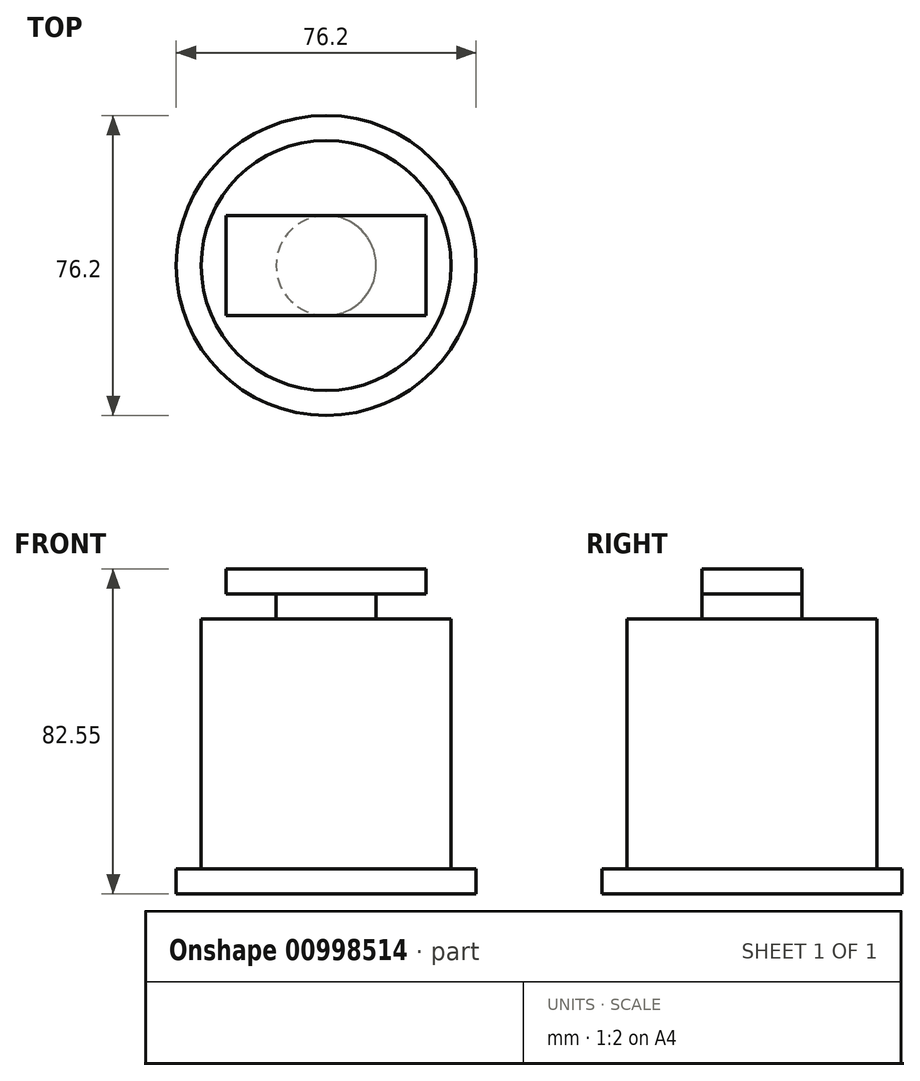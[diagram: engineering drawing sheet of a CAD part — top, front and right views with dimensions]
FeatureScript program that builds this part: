
annotation { "Feature Type Name" : "Feature", "Feature Type Description" : "" }
export const myFeature = defineFeature(function(context is Context, id is Id, definition is map)
    precondition{}
    {
        {
            var Q0;
            Q0=qCreatedBy(makeId("Top.planeOp"),FACE);
            var sketch = newSketch(context, id + "F0", { "sketchPlane" : qUnion([Q0])});
            skCircle(sketch, "E0", {"center": v(0, 0) * mm, "radius": 38.1 * mm});
            skSolve(sketch);
        }
        {
            var Q0;
            Q0=makeQuery(id+"F0.imprint","IMPRINT",FACE,{"disambiguationData":[TD([[makeQuery(id+"F0.imprint","IMPRINT",EDGE,{"derivedFrom":sQuery(id+"F0.wireOp",EDGE,"E0")}),1.0]])]});
            extrude(context, id + "F1", {"entities" : qUnion([Q0]), "depth" : 6.35 * mm, "offsetDistance" : 25.4 * mm});
        }
        {
            var Q0;
            Q0=makeQuery(id+"F1.opExtrude","CAP_FACE",FACE,{"disambiguationData":[OSD([sQuery(id+"F0.wireOp",EDGE,"E0")])],"isStart":false});
            var sketch = newSketch(context, id + "F2", { "sketchPlane" : qUnion([Q0])});
            skCircle(sketch, "E1", {"center": v(0, 0) * mm, "radius": 31.75 * mm});
            skSolve(sketch);
        }
        {
            var Q0;
            Q0=makeQuery(id+"F2.imprint","IMPRINT",FACE,{"disambiguationData":[TD([[makeQuery(id+"F2.imprint","IMPRINT",EDGE,{"derivedFrom":sQuery(id+"F2.wireOp",EDGE,"E1")}),1.0]])]});
            extrude(context, id + "F3", {"entities" : qUnion([Q0]), "operationType" : NewBodyOperationType.ADD, "depth" : 63.5 * mm, "offsetDistance" : 25.4 * mm});
        }
        {
            var Q0;
            Q0=makeQuery(id+"F3.opExtrude","CAP_FACE",FACE,{"disambiguationData":[OSD([sQuery(id+"F2.wireOp",EDGE,"E1")])],"isStart":false});
            var sketch = newSketch(context, id + "F4", { "sketchPlane" : qUnion([Q0])});
            skCircle(sketch, "E2", {"center": v(0, 0) * mm, "radius": 12.7 * mm});
            skSolve(sketch);
        }
        {
            var Q0;
            Q0=makeQuery(id+"F4.imprint","IMPRINT",FACE,{"disambiguationData":[TD([[makeQuery(id+"F4.imprint","IMPRINT",EDGE,{"derivedFrom":sQuery(id+"F4.wireOp",EDGE,"E2")}),1.0]])]});
            extrude(context, id + "F5", {"entities" : qUnion([Q0]), "depth" : 6.35 * mm, "offsetDistance" : 25.4 * mm});
        }
        {
            var Q0;
            Q0=makeQuery(id+"F5.opExtrude","CAP_FACE",FACE,{"disambiguationData":[OSD([sQuery(id+"F4.wireOp",EDGE,"E2")])],"isStart":false});
            var sketch = newSketch(context, id + "F6", { "sketchPlane" : qUnion([Q0])});
            skLineSegment(sketch, "E3.bottom", {"start": v(25.4, 12.7) * mm, "end": v(-25.4, 12.7) * mm});
            skLineSegment(sketch, "E3.top", {"start": v(25.4, -12.7) * mm, "end": v(-25.4, -12.7) * mm});
            skLineSegment(sketch, "E3.left", {"start": v(25.4, 12.7) * mm, "end": v(25.4, -12.7) * mm});
            skLineSegment(sketch, "E3.right", {"start": v(-25.4, 12.7) * mm, "end": v(-25.4, -12.7) * mm});
            skPoint(sketch, "E3.middle", {"position": v(0, 0) * mm});
            skSolve(sketch);
        }
        {
            var Q0;
            Q0 = qSketchRegion(id + "F6", true);
            extrude(context, id + "F7", {"entities" : qUnion([Q0]), "operationType" : NewBodyOperationType.ADD, "depth" : 6.35 * mm, "offsetDistance" : 25.4 * mm});
        }
    });
